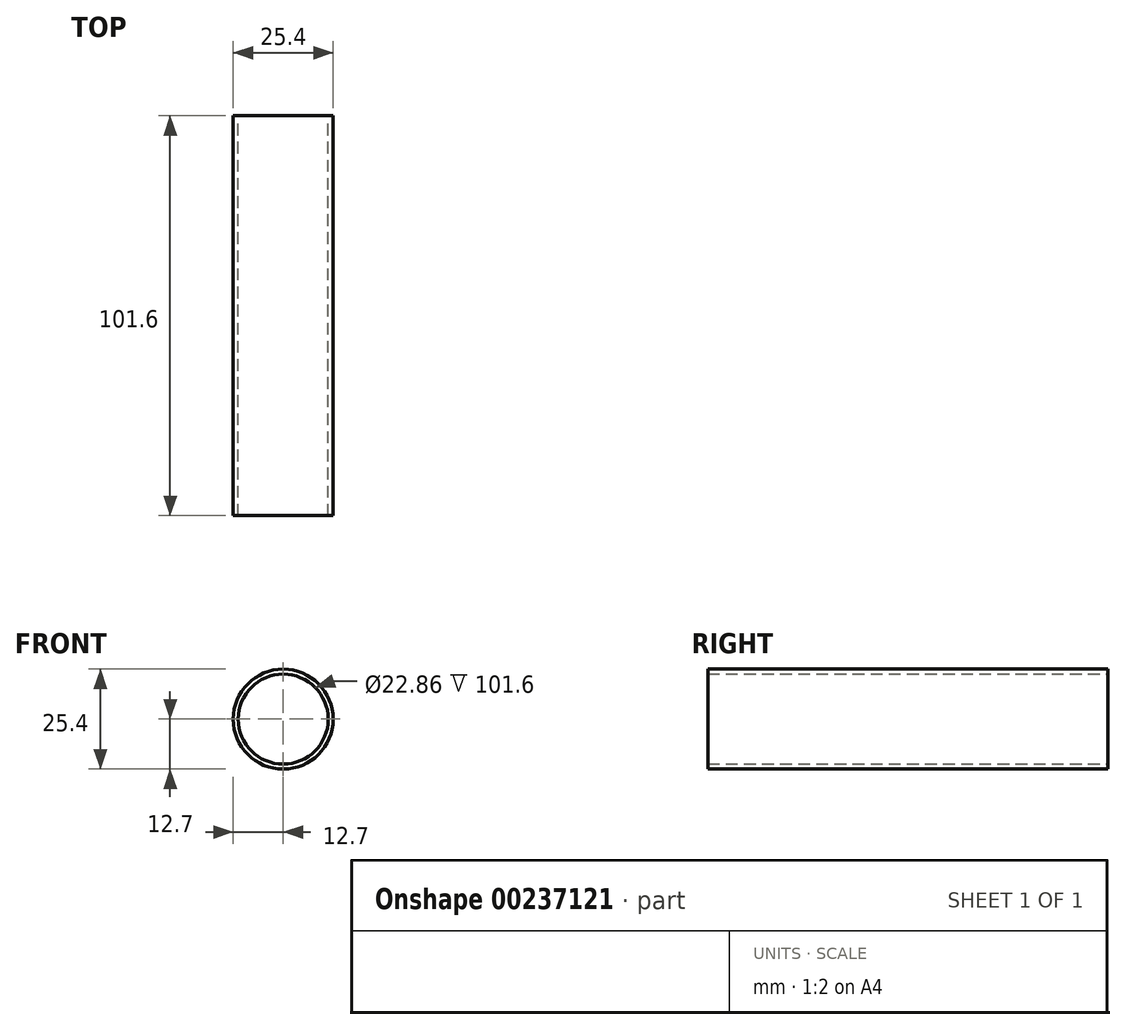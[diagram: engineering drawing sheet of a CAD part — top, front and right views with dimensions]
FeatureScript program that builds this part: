
annotation { "Feature Type Name" : "Feature", "Feature Type Description" : "" }
export const myFeature = defineFeature(function(context is Context, id is Id, definition is map)
    precondition{}
    {
        {
            var Q0;
            Q0=qCreatedBy(makeId("Front.planeOp"),FACE);
            var sketch = newSketch(context, id + "F0", { "sketchPlane" : qUnion([Q0])});
            skCircle(sketch, "E0", {"center": v(0, 0) * mm, "radius": 12.7 * mm});
            skCircle(sketch, "E1.0", {"center": v(0, 0) * mm, "radius": 11.43 * mm});
            skSolve(sketch);
        }
        {
            var Q0;
            Q0 = qSketchRegion(id + "F0", true);
            extrude(context, id + "F1", {"entities" : qUnion([Q0]), "depth" : 101.6 * mm, "symmetric" : true});
        }
    });
